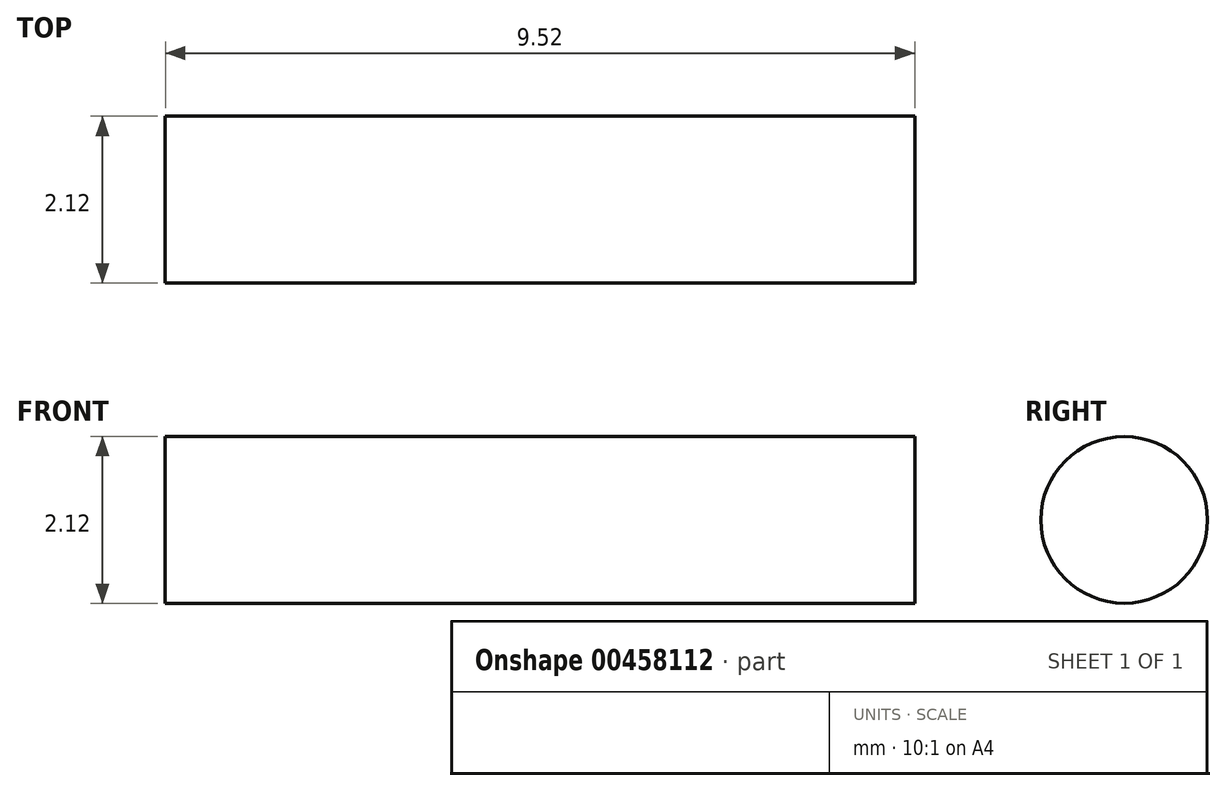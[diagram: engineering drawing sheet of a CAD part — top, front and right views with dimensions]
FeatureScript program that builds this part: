
annotation { "Feature Type Name" : "Feature", "Feature Type Description" : "" }
export const myFeature = defineFeature(function(context is Context, id is Id, definition is map)
    precondition{}
    {
        {
            var Q0;
            Q0=qCreatedBy(makeId("Right.planeOp"),FACE);
            var sketch = newSketch(context, id + "F0", { "sketchPlane" : qUnion([Q0])});
            skCircle(sketch, "E0", {"center": v(0, 0) * mm, "radius": 1.06 * mm});
            skSolve(sketch);
        }
        {
            var Q0;
            Q0=makeQuery(id+"F0.imprint","IMPRINT",FACE,{"disambiguationData":[TD([[makeQuery(id+"F0.imprint","IMPRINT",EDGE,{"derivedFrom":sQuery(id+"F0.wireOp",EDGE,"E0")}),1.0]])]});
            extrude(context, id + "F1", {"entities" : qUnion([Q0]), "endBound" : BoundingType.SYMMETRIC, "depth" : 9.52 * mm});
        }
    });
